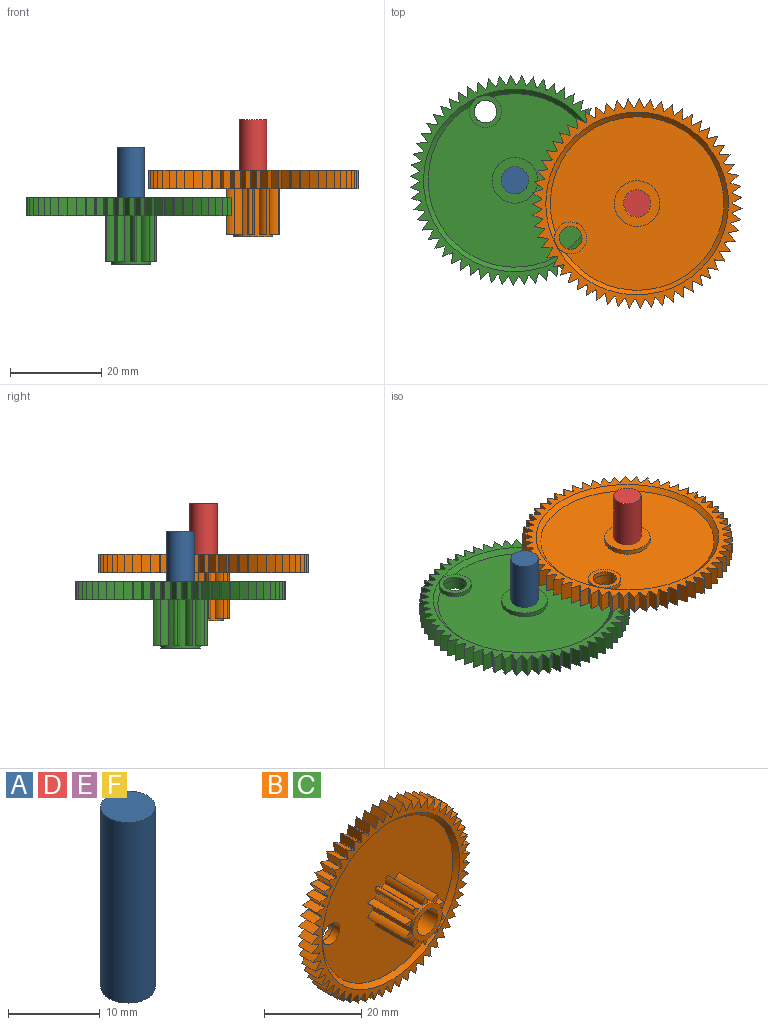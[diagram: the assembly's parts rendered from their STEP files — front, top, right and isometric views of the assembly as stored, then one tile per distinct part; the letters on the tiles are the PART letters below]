
ASSEMBLY  parts=6 mates=2
PART A: 3 faces, bbox 6x6x24.1 mm
  f0: plane 5.98x5.98mm, normal (0,0,1), area 28mm2, adj f1
  f1: cylinder r=2.99mm len=24.13mm, axis (0,0,1), area 452.9mm2, adj f0,f2
  f2: plane 5.98x5.98mm, normal (0,0,-1), area 28mm2, adj f1
PART B: 228 faces, bbox 46x14.6x46 mm
  f0: plane 4.63x3.92mm, normal (0,1,0), area 0.1mm2, adj f223,f225
  f1: plane 1.63x1.59mm, normal (0,-1,0), area 1.5mm2, adj f13,f26,f27,f222
  f2: plane 1.89x1.46mm, normal (0,-1,0), area 1.6mm2, adj f13,f24,f25
  f3: plane 1.89x1.46mm, normal (0,-1,0), area 1.6mm2, adj f13,f22,f23
  f4: plane 1.83x1.62mm, normal (0,-1,0), area 1.6mm2, adj f13,f20,f21
  f5: plane 1.76x1.4mm, normal (0,-1,0), area 1.6mm2, adj f13,f18,f19
  f6: plane 1.63x1.59mm, normal (0,-1,0), area 1.5mm2, adj f13,f16,f17,f221
  f7: plane 1.89x1.46mm, normal (0,-1,0), area 1.6mm2, adj f13,f14,f15
  f8: plane 1.89x1.46mm, normal (0,-1,0), area 1.6mm2, adj f10,f11,f13
  f9: plane 1.83x1.62mm, normal (0,-1,0), area 1.6mm2, adj f13,f30,f31
  f10: cylinder r=2.56mm len=11mm, axis (0,1,0), area 21.3mm2, adj f8,f11,f13,f214
  f11: cylinder r=2.56mm len=11mm, axis (0,1,0), area 21.3mm2, adj f8,f10,f13,f214
  f12: plane 1.76x1.4mm, normal (0,-1,0), area 1.6mm2, adj f13,f28,f29
  f13: cylinder r=4.3mm len=11.6mm, axis (0,1,0), area 158.9mm2, adj f1,f2,f3,f4,f5,f6,f7,f8
  f14: cylinder r=2.56mm len=11mm, axis (0,1,0), area 21.3mm2, adj f7,f13,f15,f214
  f15: cylinder r=2.56mm len=11mm, axis (0,1,0), area 21.3mm2, adj f7,f13,f14,f214
  f16: cylinder r=2.56mm len=11mm, axis (0,1,0), area 12.5mm2, adj f6,f13,f214,f221
  f17: cylinder r=2.56mm len=11mm, axis (0,1,0), area 12.5mm2, adj f6,f13,f214,f221
  f18: cylinder r=2.56mm len=11mm, axis (0,1,0), area 21.3mm2, adj f5,f13,f19,f214
  f19: cylinder r=2.56mm len=11mm, axis (0,1,0), area 21.3mm2, adj f5,f13,f18,f214
  f20: cylinder r=2.56mm len=11mm, axis (0,1,0), area 21.3mm2, adj f4,f13,f21,f214
  f21: cylinder r=2.56mm len=11mm, axis (0,1,0), area 21.3mm2, adj f4,f13,f20,f214
  f22: cylinder r=2.56mm len=11mm, axis (0,1,0), area 21.3mm2, adj f3,f13,f23,f214
  f23: cylinder r=2.56mm len=11mm, axis (0,1,0), area 21.3mm2, adj f3,f13,f22,f214
  f24: cylinder r=2.56mm len=11mm, axis (0,1,0), area 21.3mm2, adj f2,f13,f25,f214
  f25: cylinder r=2.56mm len=11mm, axis (0,1,0), area 21.3mm2, adj f2,f13,f24,f214
  f26: cylinder r=2.56mm len=11mm, axis (0,1,0), area 12.5mm2, adj f1,f13,f214,f222
  f27: cylinder r=2.56mm len=11mm, axis (0,1,0), area 12.5mm2, adj f1,f13,f214,f222
  f28: cylinder r=2.56mm len=11mm, axis (0,1,0), area 21.3mm2, adj f12,f13,f29,f214
  f29: cylinder r=2.56mm len=11mm, axis (0,1,0), area 21.3mm2, adj f12,f13,f28,f214
  f30: cylinder r=2.56mm len=11mm, axis (0,1,0), area 21.3mm2, adj f9,f13,f31,f214
  f31: cylinder r=2.56mm len=11mm, axis (0,1,0), area 21.3mm2, adj f9,f13,f30,f214
  f32: cylinder r=3mm len=13.6mm, axis (0,1,0), area 256.4mm2, adj f33,f215
  f33: plane 8.6x8.6mm, normal (0,-1,0), area 29.8mm2, adj f13,f32
  f34: cylinder r=21mm len=4mm, axis (0,1,0), area 0.9mm2, adj f93,f94,f97,f212
  f35: cylinder r=21mm len=4mm, axis (0,1,0), area 0.9mm2, adj f93,f94,f210,f213
  f36: cylinder r=21mm len=4mm, axis (0,1,0), area 0.9mm2, adj f93,f94,f208,f211
  f37: cylinder r=21mm len=4mm, axis (0,1,0), area 0.9mm2, adj f93,f94,f206,f209
  f38: cylinder r=21mm len=4mm, axis (0,1,0), area 0.9mm2, adj f93,f94,f204,f207
  f39: cylinder r=21mm len=4mm, axis (0,1,0), area 0.9mm2, adj f93,f94,f202,f205
  f40: cylinder r=21mm len=4mm, axis (0,1,0), area 0.9mm2, adj f93,f94,f200,f203
  f41: cylinder r=21mm len=4mm, axis (0,1,0), area 0.9mm2, adj f93,f94,f198,f201
  f42: cylinder r=21mm len=4mm, axis (0,1,0), area 0.9mm2, adj f93,f94,f196,f199
  f43: cylinder r=21mm len=4mm, axis (0,1,0), area 0.9mm2, adj f93,f94,f194,f197
  f44: cylinder r=21mm len=4mm, axis (0,1,0), area 0.9mm2, adj f93,f94,f192,f195
  f45: cylinder r=21mm len=4mm, axis (0,1,0), area 0.9mm2, adj f93,f94,f190,f193
  f46: cylinder r=21mm len=4mm, axis (0,1,0), area 0.9mm2, adj f93,f94,f188,f191
  f47: cylinder r=21mm len=4mm, axis (0,1,0), area 0.9mm2, adj f93,f94,f186,f189
  f48: cylinder r=21mm len=4mm, axis (0,1,0), area 0.9mm2, adj f93,f94,f184,f187
  f49: cylinder r=21mm len=4mm, axis (0,1,0), area 0.9mm2, adj f93,f94,f182,f185
  f50: cylinder r=21mm len=4mm, axis (0,1,0), area 0.9mm2, adj f93,f94,f180,f183
  f51: cylinder r=21mm len=4mm, axis (0,1,0), area 0.9mm2, adj f93,f94,f178,f181
  f52: cylinder r=21mm len=4mm, axis (0,1,0), area 0.9mm2, adj f93,f94,f176,f179
  f53: cylinder r=21mm len=4mm, axis (0,1,0), area 0.9mm2, adj f93,f94,f174,f177
  f54: cylinder r=21mm len=4mm, axis (0,1,0), area 0.9mm2, adj f93,f94,f172,f175
  f55: cylinder r=21mm len=4mm, axis (0,1,0), area 0.9mm2, adj f93,f94,f170,f173
  f56: cylinder r=21mm len=4mm, axis (0,1,0), area 0.9mm2, adj f93,f94,f168,f171
  f57: cylinder r=21mm len=4mm, axis (0,1,0), area 0.9mm2, adj f93,f94,f166,f169
  f58: cylinder r=21mm len=4mm, axis (0,1,0), area 0.9mm2, adj f93,f94,f164,f167
  f59: cylinder r=21mm len=4mm, axis (0,1,0), area 0.9mm2, adj f93,f94,f162,f165
  f60: cylinder r=21mm len=4mm, axis (0,1,0), area 0.9mm2, adj f93,f94,f160,f163
  f61: cylinder r=21mm len=4mm, axis (0,1,0), area 0.9mm2, adj f93,f94,f158,f161
  f62: cylinder r=21mm len=4mm, axis (0,1,0), area 0.9mm2, adj f93,f94,f156,f159
  f63: cylinder r=21mm len=4mm, axis (0,1,0), area 0.9mm2, adj f93,f94,f154,f157
  f64: cylinder r=21mm len=4mm, axis (0,1,0), area 0.9mm2, adj f93,f94,f152,f155
  f65: cylinder r=21mm len=4mm, axis (0,1,0), area 0.9mm2, adj f93,f94,f150,f153
  f66: cylinder r=21mm len=4mm, axis (0,1,0), area 0.9mm2, adj f93,f94,f148,f151
  f67: cylinder r=21mm len=4mm, axis (0,1,0), area 0.9mm2, adj f93,f94,f146,f149
  f68: cylinder r=21mm len=4mm, axis (0,1,0), area 0.9mm2, adj f93,f94,f144,f147
  f69: cylinder r=21mm len=4mm, axis (0,1,0), area 0.9mm2, adj f93,f94,f142,f145
  f70: cylinder r=21mm len=4mm, axis (0,1,0), area 0.9mm2, adj f93,f94,f140,f143
  f71: cylinder r=21mm len=4mm, axis (0,1,0), area 0.9mm2, adj f93,f94,f138,f141
  f72: cylinder r=21mm len=4mm, axis (0,1,0), area 0.9mm2, adj f93,f94,f136,f139
  f73: cylinder r=21mm len=4mm, axis (0,1,0), area 0.9mm2, adj f93,f94,f134,f137
  f74: cylinder r=21mm len=4mm, axis (0,1,0), area 0.9mm2, adj f93,f94,f132,f135
  f75: cylinder r=21mm len=4mm, axis (0,1,0), area 0.9mm2, adj f93,f94,f130,f133
  f76: cylinder r=21mm len=4mm, axis (0,1,0), area 0.9mm2, adj f93,f94,f128,f131
  f77: cylinder r=21mm len=4mm, axis (0,1,0), area 0.9mm2, adj f93,f94,f126,f129
  f78: cylinder r=21mm len=4mm, axis (0,1,0), area 0.9mm2, adj f93,f94,f124,f127
  f79: cylinder r=21mm len=4mm, axis (0,1,0), area 0.9mm2, adj f93,f94,f122,f125
  f80: cylinder r=21mm len=4mm, axis (0,1,0), area 0.9mm2, adj f93,f94,f120,f123
  f81: cylinder r=21mm len=4mm, axis (0,1,0), area 0.9mm2, adj f93,f94,f118,f121
  f82: cylinder r=21mm len=4mm, axis (0,1,0), area 0.9mm2, adj f93,f94,f116,f119
  f83: cylinder r=21mm len=4mm, axis (0,1,0), area 0.9mm2, adj f93,f94,f114,f117
  f84: cylinder r=21mm len=4mm, axis (0,1,0), area 0.9mm2, adj f93,f94,f112,f115
  f85: cylinder r=21mm len=4mm, axis (0,1,0), area 0.9mm2, adj f93,f94,f110,f113
  f86: cylinder r=21mm len=4mm, axis (0,1,0), area 0.9mm2, adj f93,f94,f108,f111
  f87: cylinder r=21mm len=4mm, axis (0,1,0), area 0.9mm2, adj f93,f94,f106,f109
  f88: cylinder r=21mm len=4mm, axis (0,1,0), area 0.9mm2, adj f93,f94,f104,f107
  f89: cylinder r=21mm len=4mm, axis (0,1,0), area 0.9mm2, adj f93,f94,f102,f105
  f90: cylinder r=21mm len=4mm, axis (0,1,0), area 0.9mm2, adj f93,f94,f100,f103
  f91: cylinder r=21mm len=4mm, axis (0,1,0), area 0.9mm2, adj f93,f94,f98,f101
  f92: cylinder r=21mm len=4mm, axis (0,1,0), area 0.9mm2, adj f93,f94,f96,f99
  f93: plane 45.98x45.97mm, normal (0,-1,0), area 246.3mm2, adj f34,f35,f36,f37,f38,f39,f40,f41
  f94: plane 45.98x45.97mm, normal (0,1,0), area 246.3mm2, adj f34,f35,f36,f37,f38,f39,f40,f41
  f95: plane 38x37.91mm, normal (0,1,0), area 1020.2mm2, adj f217,f220,f226
  f96: plane 4x2.02mm, normal (-0.9,0,-0.44), area 9mm2, adj f92,f93,f94,f97
  f97: plane 4x2.02mm, normal (0.9,0,-0.44), area 9mm2, adj f34,f93,f94,f96
  f98: plane 4x2.12mm, normal (-0.94,0,-0.35), area 9mm2, adj f91,f93,f94,f99
  f99: plane 4x1.91mm, normal (0.84,0,-0.54), area 9mm2, adj f92,f93,f94,f98
  f100: plane 4x2.19mm, normal (-0.97,0,-0.24), area 9mm2, adj f90,f93,f94,f101
  f101: plane 4x1.77mm, normal (0.78,0,-0.62), area 9mm2, adj f91,f93,f94,f100
  f102: plane 4x2.24mm, normal (-0.99,0,-0.14), area 9mm2, adj f89,f93,f94,f103
  f103: plane 4x1.61mm, normal (0.71,0,-0.7), area 9mm2, adj f90,f93,f94,f102
  f104: plane 4x2.26mm, normal (-1,0,-0.03), area 9mm2, adj f88,f93,f94,f105
  f105: plane 4x1.75mm, normal (0.63,0,-0.77), area 9mm2, adj f89,f93,f94,f104
  f106: plane 4x2.25mm, normal (-1,0,0.07), area 9mm2, adj f87,f93,f94,f107
  f107: plane 4x1.89mm, normal (0.55,0,-0.84), area 9mm2, adj f88,f93,f94,f106
  f108: plane 4x2.22mm, normal (-0.98,0,0.18), area 9mm2, adj f86,f93,f94,f109
  f109: plane 4x2.01mm, normal (0.46,0,-0.89), area 9mm2, adj f87,f93,f94,f108
  f110: plane 4x2.17mm, normal (-0.96,0,0.28), area 9mm2, adj f85,f93,f94,f111
  f111: plane 4x2.11mm, normal (0.36,0,-0.93), area 9mm2, adj f86,f93,f94,f110
  f112: plane 4x2.09mm, normal (-0.92,0,0.38), area 9mm2, adj f84,f93,f94,f113
  f113: plane 4x2.18mm, normal (0.26,0,-0.97), area 9mm2, adj f85,f93,f94,f112
  f114: plane 4x1.98mm, normal (-0.88,0,0.48), area 9mm2, adj f83,f93,f94,f115
  f115: plane 4x2.23mm, normal (0.15,0,-0.99), area 9mm2, adj f84,f93,f94,f114
  f116: plane 4x1.86mm, normal (-0.82,0,0.57), area 9mm2, adj f82,f93,f94,f117
  f117: plane 4x2.26mm, normal (0.05,0,-1), area 9mm2, adj f83,f93,f94,f116
  f118: plane 4x1.71mm, normal (-0.76,0,0.65), area 9mm2, adj f81,f93,f94,f119
  f119: plane 4x2.25mm, normal (-0.06,0,-1), area 9mm2, adj f82,f93,f94,f118
  f120: plane 4x1.65mm, normal (-0.68,0,0.73), area 9mm2, adj f80,f93,f94,f121
  f121: plane 4x2.23mm, normal (-0.17,0,-0.99), area 9mm2, adj f81,f93,f94,f120
  f122: plane 4x1.8mm, normal (-0.6,0,0.8), area 9mm2, adj f79,f93,f94,f123
  f123: plane 4x2.17mm, normal (-0.27,0,-0.96), area 9mm2, adj f80,f93,f94,f122
  f124: plane 4x1.94mm, normal (-0.51,0,0.86), area 9mm2, adj f78,f93,f94,f125
  f125: plane 4x2.1mm, normal (-0.37,0,-0.93), area 9mm2, adj f79,f93,f94,f124
  f126: plane 4x2.05mm, normal (-0.42,0,0.91), area 9mm2, adj f77,f93,f94,f127
  f127: plane 4x2mm, normal (-0.47,0,-0.88), area 9mm2, adj f78,f93,f94,f126
  f128: plane 4x2.14mm, normal (-0.32,0,0.95), area 9mm2, adj f76,f93,f94,f129
  f129: plane 4x1.87mm, normal (-0.56,0,-0.83), area 9mm2, adj f77,f93,f94,f128
  f130: plane 4x2.2mm, normal (-0.22,0,0.98), area 9mm2, adj f75,f93,f94,f131
  f131: plane 4x1.73mm, normal (-0.64,0,-0.77), area 9mm2, adj f76,f93,f94,f130
  f132: plane 4x2.24mm, normal (-0.11,0,0.99), area 9mm2, adj f74,f93,f94,f133
  f133: plane 4x1.63mm, normal (-0.72,0,-0.69), area 9mm2, adj f75,f93,f94,f132
  f134: plane 4x2.26mm, normal (-0.01,0,1), area 9mm2, adj f73,f93,f94,f135
  f135: plane 4x1.78mm, normal (-0.79,0,-0.61), area 9mm2, adj f74,f93,f94,f134
  f136: plane 4x2.25mm, normal (0.1,0,0.99), area 9mm2, adj f72,f93,f94,f137
  f137: plane 4x1.92mm, normal (-0.85,0,-0.53), area 9mm2, adj f73,f93,f94,f136
  f138: plane 4x2.21mm, normal (0.21,0,0.98), area 9mm2, adj f71,f93,f94,f139
  f139: plane 4x2.04mm, normal (-0.9,0,-0.43), area 9mm2, adj f72,f93,f94,f138
  f140: plane 4x2.15mm, normal (0.31,0,0.95), area 9mm2, adj f70,f93,f94,f141
  f141: plane 4x2.13mm, normal (-0.94,0,-0.33), area 9mm2, adj f71,f93,f94,f140
  f142: plane 4x2.06mm, normal (0.41,0,0.91), area 9mm2, adj f69,f93,f94,f143
  f143: plane 4x2.2mm, normal (-0.97,0,-0.23), area 9mm2, adj f70,f93,f94,f142
  f144: plane 4x1.95mm, normal (0.5,0,0.86), area 9mm2, adj f68,f93,f94,f145
  f145: plane 4x2.24mm, normal (-0.99,0,-0.13), area 9mm2, adj f69,f93,f94,f144
  f146: plane 4x1.82mm, normal (0.59,0,0.81), area 9mm2, adj f67,f93,f94,f147
  f147: plane 4x2.26mm, normal (-1,0,-0.02), area 9mm2, adj f68,f93,f94,f146
  f148: plane 4x1.67mm, normal (0.67,0,0.74), area 9mm2, adj f66,f93,f94,f149
  f149: plane 4x2.25mm, normal (-1,0,0.09), area 9mm2, adj f67,f93,f94,f148
  f150: plane 4x1.69mm, normal (0.75,0,0.66), area 9mm2, adj f65,f93,f94,f151
  f151: plane 4x2.22mm, normal (-0.98,0,0.19), area 9mm2, adj f66,f93,f94,f150
  f152: plane 4x1.84mm, normal (0.81,0,0.58), area 9mm2, adj f64,f93,f94,f153
  f153: plane 4x2.16mm, normal (-0.96,0,0.29), area 9mm2, adj f65,f93,f94,f152
  f154: plane 4x1.97mm, normal (0.87,0,0.49), area 9mm2, adj f63,f93,f94,f155
  f155: plane 4x2.07mm, normal (-0.92,0,0.39), area 9mm2, adj f64,f93,f94,f154
  f156: plane 4x2.07mm, normal (0.92,0,0.39), area 9mm2, adj f62,f93,f94,f157
  f157: plane 4x1.97mm, normal (-0.87,0,0.49), area 9mm2, adj f63,f93,f94,f156
  f158: plane 4x2.16mm, normal (0.96,0,0.29), area 9mm2, adj f61,f93,f94,f159
  f159: plane 4x1.84mm, normal (-0.81,0,0.58), area 9mm2, adj f62,f93,f94,f158
  f160: plane 4x2.22mm, normal (0.98,0,0.19), area 9mm2, adj f60,f93,f94,f161
  f161: plane 4x1.69mm, normal (-0.75,0,0.66), area 9mm2, adj f61,f93,f94,f160
  f162: plane 4x2.25mm, normal (1,0,0.09), area 9mm2, adj f59,f93,f94,f163
  f163: plane 4x1.67mm, normal (-0.67,0,0.74), area 9mm2, adj f60,f93,f94,f162
  f164: plane 4x2.26mm, normal (1,0,-0.02), area 9mm2, adj f58,f93,f94,f165
  f165: plane 4x1.82mm, normal (-0.59,0,0.81), area 9mm2, adj f59,f93,f94,f164
  f166: plane 4x2.24mm, normal (0.99,0,-0.13), area 9mm2, adj f57,f93,f94,f167
  f167: plane 4x1.95mm, normal (-0.5,0,0.86), area 9mm2, adj f58,f93,f94,f166
  f168: plane 4x2.2mm, normal (0.97,0,-0.23), area 9mm2, adj f56,f93,f94,f169
  f169: plane 4x2.06mm, normal (-0.41,0,0.91), area 9mm2, adj f57,f93,f94,f168
  f170: plane 4x2.13mm, normal (0.94,0,-0.33), area 9mm2, adj f55,f93,f94,f171
  f171: plane 4x2.15mm, normal (-0.31,0,0.95), area 9mm2, adj f56,f93,f94,f170
  f172: plane 4x2.04mm, normal (0.9,0,-0.43), area 9mm2, adj f54,f93,f94,f173
  f173: plane 4x2.21mm, normal (-0.21,0,0.98), area 9mm2, adj f55,f93,f94,f172
  f174: plane 4x1.92mm, normal (0.85,0,-0.53), area 9mm2, adj f53,f93,f94,f175
  f175: plane 4x2.25mm, normal (-0.1,0,0.99), area 9mm2, adj f54,f93,f94,f174
  f176: plane 4x1.78mm, normal (0.79,0,-0.61), area 9mm2, adj f52,f93,f94,f177
  f177: plane 4x2.26mm, normal (0.01,0,1), area 9mm2, adj f53,f93,f94,f176
  f178: plane 4x1.63mm, normal (0.72,0,-0.69), area 9mm2, adj f51,f93,f94,f179
  f179: plane 4x2.24mm, normal (0.11,0,0.99), area 9mm2, adj f52,f93,f94,f178
  f180: plane 4x1.73mm, normal (0.64,0,-0.77), area 9mm2, adj f50,f93,f94,f181
  f181: plane 4x2.2mm, normal (0.22,0,0.98), area 9mm2, adj f51,f93,f94,f180
  f182: plane 4x1.87mm, normal (0.56,0,-0.83), area 9mm2, adj f49,f93,f94,f183
  f183: plane 4x2.14mm, normal (0.32,0,0.95), area 9mm2, adj f50,f93,f94,f182
  f184: plane 4x2mm, normal (0.47,0,-0.88), area 9mm2, adj f48,f93,f94,f185
  f185: plane 4x2.05mm, normal (0.42,0,0.91), area 9mm2, adj f49,f93,f94,f184
  f186: plane 4x2.1mm, normal (0.37,0,-0.93), area 9mm2, adj f47,f93,f94,f187
  f187: plane 4x1.94mm, normal (0.51,0,0.86), area 9mm2, adj f48,f93,f94,f186
  f188: plane 4x2.17mm, normal (0.27,0,-0.96), area 9mm2, adj f46,f93,f94,f189
  f189: plane 4x1.8mm, normal (0.6,0,0.8), area 9mm2, adj f47,f93,f94,f188
  f190: plane 4x2.23mm, normal (0.17,0,-0.99), area 9mm2, adj f45,f93,f94,f191
  f191: plane 4x1.65mm, normal (0.68,0,0.73), area 9mm2, adj f46,f93,f94,f190
  f192: plane 4x2.25mm, normal (0.06,0,-1), area 9mm2, adj f44,f93,f94,f193
  f193: plane 4x1.71mm, normal (0.76,0,0.65), area 9mm2, adj f45,f93,f94,f192
  f194: plane 4x2.26mm, normal (-0.05,0,-1), area 9mm2, adj f43,f93,f94,f195
  f195: plane 4x1.86mm, normal (0.82,0,0.57), area 9mm2, adj f44,f93,f94,f194
  f196: plane 4x2.23mm, normal (-0.15,0,-0.99), area 9mm2, adj f42,f93,f94,f197
  f197: plane 4x1.98mm, normal (0.88,0,0.48), area 9mm2, adj f43,f93,f94,f196
  f198: plane 4x2.18mm, normal (-0.26,0,-0.97), area 9mm2, adj f41,f93,f94,f199
  f199: plane 4x2.09mm, normal (0.92,0,0.38), area 9mm2, adj f42,f93,f94,f198
  f200: plane 4x2.11mm, normal (-0.36,0,-0.93), area 9mm2, adj f40,f93,f94,f201
  f201: plane 4x2.17mm, normal (0.96,0,0.28), area 9mm2, adj f41,f93,f94,f200
  f202: plane 4x2.01mm, normal (-0.46,0,-0.89), area 9mm2, adj f39,f93,f94,f203
  f203: plane 4x2.22mm, normal (0.98,0,0.18), area 9mm2, adj f40,f93,f94,f202
  f204: plane 4x1.89mm, normal (-0.55,0,-0.84), area 9mm2, adj f38,f93,f94,f205
  f205: plane 4x2.25mm, normal (1,0,0.07), area 9mm2, adj f39,f93,f94,f204
  f206: plane 4x1.75mm, normal (-0.63,0,-0.77), area 9mm2, adj f37,f93,f94,f207
  f207: plane 4x2.26mm, normal (1,0,-0.03), area 9mm2, adj f38,f93,f94,f206
  f208: plane 4x1.61mm, normal (-0.71,0,-0.7), area 9mm2, adj f36,f93,f94,f209
  f209: plane 4x2.24mm, normal (0.99,0,-0.14), area 9mm2, adj f37,f93,f94,f208
  f210: plane 4x1.77mm, normal (-0.78,0,-0.62), area 9mm2, adj f35,f93,f94,f211
  f211: plane 4x2.19mm, normal (0.97,0,-0.24), area 9mm2, adj f36,f93,f94,f210
  f212: plane 4x1.91mm, normal (-0.84,0,-0.54), area 9mm2, adj f34,f93,f94,f213
  f213: plane 4x2.12mm, normal (0.94,0,-0.35), area 9mm2, adj f35,f93,f94,f212
  f214: plane 38x38mm, normal (0,-1,0), area 1040.3mm2, adj f10,f11,f13,f14,f15,f16,f17,f18
  f215: plane 6x6mm, normal (0,-1,0), area 8.6mm2, adj f32,f218
  f216: plane 10x10mm, normal (0,1,0), area 58.9mm2, adj f217,f218
  f217: cylinder r=5mm len=10mm, axis (0,-1,0), area 31.4mm2, adj f95,f216
  f218: cylinder r=2.5mm len=5mm, axis (0,-1,0), area 15.7mm2, adj f215,f216
  f219: cone r=19mm half-angle=45deg, axis (0,-1,0), area 173.3mm2, adj f93,f214
  f220: cone r=20mm half-angle=45deg, axis (0,1,0), area 168.8mm2, adj f94,f95,f226
  f221: cylinder r=0.5mm len=11mm, axis (0,1,0), area 12.4mm2, adj f6,f16,f17,f214
  f222: cylinder r=0.5mm len=11mm, axis (0,1,0), area 12.4mm2, adj f1,f26,f27,f214
  f223: cylinder r=2.5mm len=5mm, axis (0,-1,0), area 31.4mm2, adj f0,f214,f224
  f224: plane 4.57x3.83mm, normal (0,-1,0), area 0.1mm2, adj f223,f225
  f225: cylinder r=2.5mm len=5mm, axis (0,1,0), area 15.7mm2, adj f0,f224,f227
  f226: cylinder r=3.5mm len=7.01mm, axis (0,1,0), area 18.7mm2, adj f95,f220,f227
  f227: plane 7.01x7.01mm, normal (0,1,0), area 18.9mm2, adj f225,f226
PART C: same geometry as B
PART D: same geometry as A
PART E: same geometry as A
PART F: same geometry as A
PLACE A t=(-43.7,30.37,-2.95)mm fixed
PLACE B rot(axis=(0.94,0.25,0.25),93.7deg) t=(-16.93,25.29,4.02)mm
PLACE C rot(axis=(0.74,-0.47,-0.47),106.7deg) t=(-43.7,30.37,-1.95)mm
PLACE D t=(-16.93,25.29,3.02)mm fixed
PLACE E t=(-16.93,25.29,3.02)mm
PLACE F t=(-16.93,25.29,3.02)mm
MATE revolute D.f1 <-> B.f13  axis (0,0,1) through (-16.93,25.29,3.02)mm
MATE revolute A.f1 <-> C.f13  axis (0,0,1) through (-43.7,30.37,-2.95)mm
